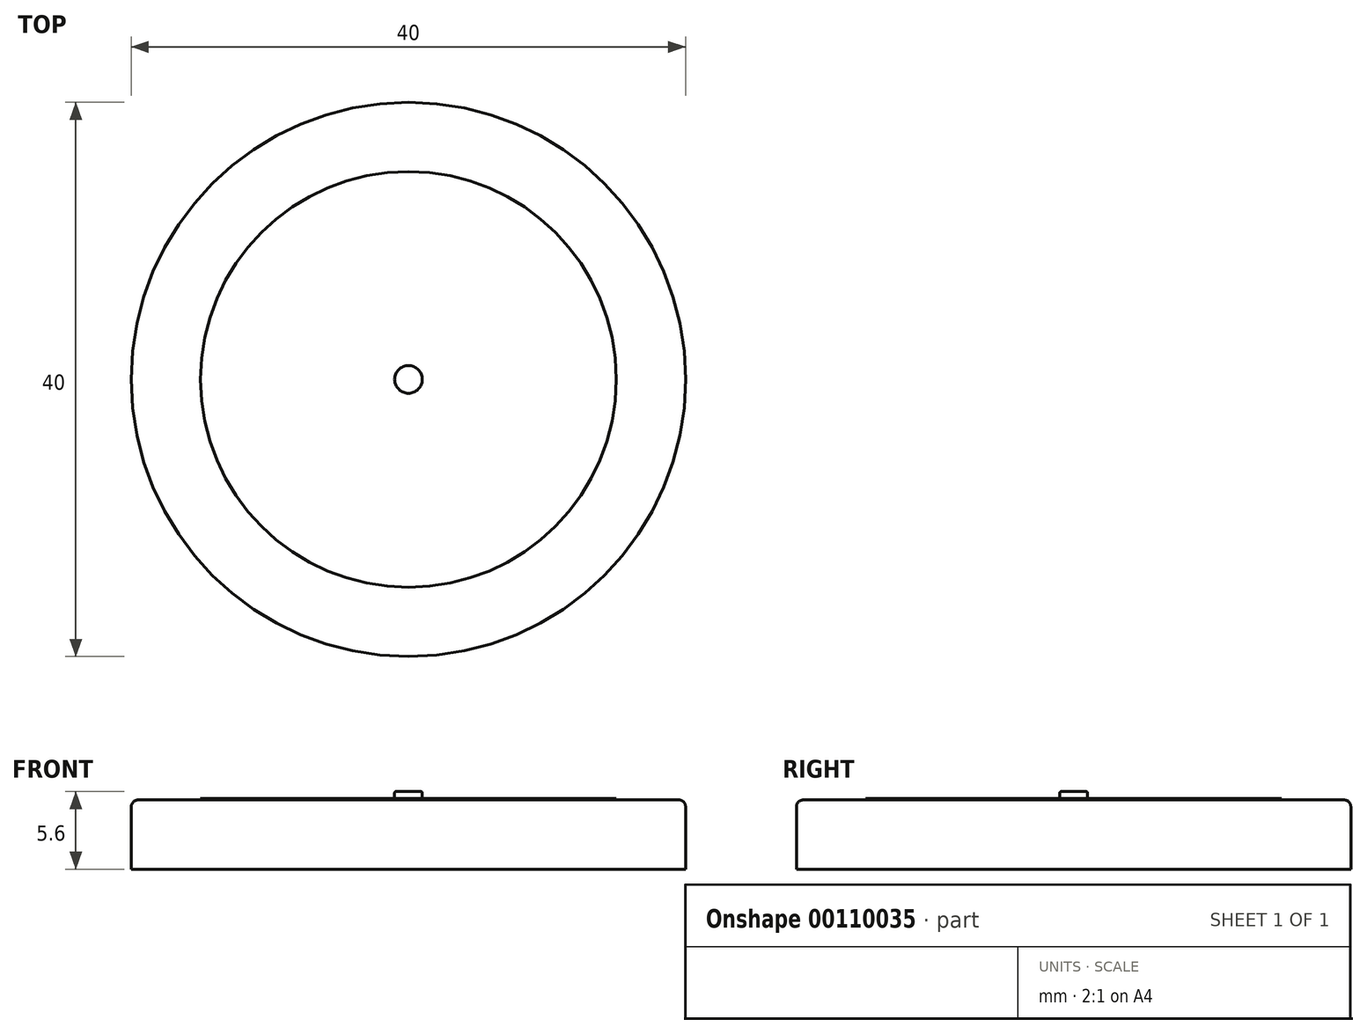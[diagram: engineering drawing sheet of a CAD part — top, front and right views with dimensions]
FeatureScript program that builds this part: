
annotation { "Feature Type Name" : "Feature", "Feature Type Description" : "" }
export const myFeature = defineFeature(function(context is Context, id is Id, definition is map)
    precondition{}
    {
        {
            var Q0;
            Q0=qCreatedBy(makeId("Top.planeOp"),FACE);
            var sketch = newSketch(context, id + "F0", { "sketchPlane" : qUnion([Q0])});
            skCircle(sketch, "E0", {"center": v(0, 0) * mm, "radius": 20 * mm});
            skSolve(sketch);
        }
        {
            var Q0;
            Q0=makeQuery(id+"F0.imprint","IMPRINT",FACE,{"disambiguationData":[TD([[makeQuery(id+"F0.imprint","IMPRINT",EDGE,{"derivedFrom":sQuery(id+"F0.wireOp",EDGE,"E0")}),1.0]])]});
            extrude(context, id + "F1", {"entities" : qUnion([Q0]), "depth" : 5 * mm});
        }
        {
            var Q0;
            Q0=makeQuery(id+"F1.opExtrude","CAP_FACE",FACE,{"disambiguationData":[OSD([sQuery(id+"F0.wireOp",EDGE,"E0")])],"isStart":false});
            var sketch = newSketch(context, id + "F2", { "sketchPlane" : qUnion([Q0])});
            skCircle(sketch, "E1", {"center": v(0, 0) * mm, "radius": 15 * mm});
            skSolve(sketch);
        }
        {
            var Q0;
            Q0=makeQuery(id+"F2.imprint","IMPRINT",FACE,{"disambiguationData":[TD([[makeQuery(id+"F2.imprint","IMPRINT",EDGE,{"derivedFrom":sQuery(id+"F2.wireOp",EDGE,"E1")}),1.0]])]});
            extrude(context, id + "F3", {"entities" : qUnion([Q0]), "operationType" : NewBodyOperationType.ADD, "depth" : 0.1 * mm});
        }
        {
            var Q0;
            Q0=makeQuery(id+"F1.opExtrude","CAP_EDGE",EDGE,{"disambiguationData":[OSD([sQuery(id+"F0.wireOp",EDGE,"E0")])],"isStart":false});
            fillet(context, id + "F4", {"entities" : qUnion([Q0]), "radius" : 0.5 * mm, "tangentPropagation" : true, "allowEdgeOverflow" : false});
        }
        {
            var Q0;
            Q0=makeQuery(id+"F3.opExtrude","CAP_FACE",FACE,{"disambiguationData":[OSD([sQuery(id+"F2.wireOp",EDGE,"E1")])],"isStart":false});
            var sketch = newSketch(context, id + "F5", { "sketchPlane" : qUnion([Q0])});
            skCircle(sketch, "E2", {"center": v(0, 0) * mm, "radius": 1 * mm});
            skSolve(sketch);
        }
        {
            var Q0;
            Q0=makeQuery(id+"F5.imprint","IMPRINT",FACE,{"disambiguationData":[TD([[makeQuery(id+"F5.imprint","IMPRINT",EDGE,{"derivedFrom":sQuery(id+"F5.wireOp",EDGE,"E2")}),1.0]])]});
            extrude(context, id + "F6", {"entities" : qUnion([Q0]), "operationType" : NewBodyOperationType.ADD, "depth" : 0.5 * mm});
        }
        {
            var Q0;
            Q0=makeQuery(id+"F6.opExtrude","CAP_EDGE",EDGE,{"disambiguationData":[OSD([sQuery(id+"F5.wireOp",EDGE,"E2")])],"isStart":false});
            fillet(context, id + "F7", {"entities" : qUnion([Q0]), "radius" : 0.1 * mm, "tangentPropagation" : true, "allowEdgeOverflow" : false});
        }
    });
